# Revit family: 1030072(n0300)
name_source: partatom
category: Security Devices
units: mm (PartAtom-declared; Revit-internal decimal feet)

## family parameters
Always vertical = No
Cut with Voids When Loaded = No
Host = Ceiling
OmniClass Number = 23.85.30.14
OmniClass Title = Presence Detection/Registration
Room Calculation Point = No
Shared = Yes

## types (2) — shared parameters
zero-valued in all types: A

## per-type parameters (varying)
- Type 1: CTN=0; EF000008=0 mm  [stored 0 ft]; EF000040=0 mm  [stored 0 ft]; EF000049=0 mm  [stored 0 ft]; EF000194=0; EF000218=0 mm  [stored 0 ft]; EF000551=0 mm  [stored 0 ft]; EF000846=0 mm  [stored 0 ft]; EF001322=0 mm  [stored 0 ft]; EF001323=0 mm  [stored 0 ft]; EF003843=0 mm  [stored 0 ft]; EF003882=0; EF004101=0.00°; EF004265=0 mm  [stored 0 ft]; EF006589=0; EF006590=0; EF008011=0 mm  [stored 0 ft]; EF010886=0 mm  [stored 0 ft]; EF010945=0 mm  [stored 0 ft]; EF010946=0 mm  [stored 0 ft]; EF012278=0 mm  [stored 0 ft]; LOG=0; NOCUPEROU=0; PRICEQUANTITY=0; QUANTITYINT=0; QUANTITYMIN=0
- 1030072: ARTICLENO=NB; BOMINFO=LINA; CATALOG=Theben; COO=CN; CTN=85365080; DEEPLINK_PRODUKTSEITE=http://www.theben.de; DESCLONG=Passive infrared presence detector for flush or surface ceiling mounting, Rectangular detection area 360° for corridors, 28x5 m, (140 square meters) at 3 m mounting height (transverse walking), 14x5 m, (70 square meters) at 3 m mounting height (frontal walking), 1 channel light (relay 230 V), Can also be used in damp rooms and outdoors due to protection class IP 54, Remote controllable, Parallel connection with other LUXA 103 or theMura Slave possible, Switching capacity optimized for LED up to 400 W, Semi- or fully automatic operation, Integrated push button input, With pulse function, teach-in function, test function and staircase lighting function, Area restriction possible with cover clips, Housing color white; DESCSHORT=Corridor presence detector ceiling mounting flush-mounted/DE, detection area 28x5 m, 1 x light; EF000003=EV000383; EF000007=White; EF000008=80 mm  [stored 0.262467 ft]; EF000010=Presence detector; EF000025=true; EF000040=80 mm  [stored 0.262467 ft]; EF000049=80 mm  [stored 0.262467 ft]; EF000124=Plug-in clamp; EF000139=Untreated; EF000147=false; EF000187=AC; EF000194=15; EF000218=49 mm  [stored 0.160761 ft]; EF000416=50, 50 Hz; EF000483=false; EF000551=80 mm  [stored 0.262467 ft]; EF000846=40 mm  [stored 0.131234 ft]; EF001098=true; EF001099=true; EF001198=false; EF001257=Thermoplast; EF001322=14000 mm; EF001323=14000 mm; EF001731=-25, 55 °C; EF002169=Plastic; EF003429=true; EF003808=false; EF003814=5, 1000 lx; EF003832=false; EF003843=140000 mm; EF003848=true; EF003858=false; EF003863=false; EF003876=true; EF003882=9010; EF003890=true; EF003898=true; EF003904=true; EF003920=false; EF004101=360.00°; EF004265=40 mm  [stored 0.131234 ft]; EF004293=IK04; EF005474=IP54; EF005624=false; EF006243=false; EF006311=false; EF006569=matt; EF006582=0, 360 °; EF006589=15; EF006590=30; EF006644=false; EF007575=true; EF008011=3000 mm; EF009569=false; EF010886=31 mm  [stored 0.101706 ft]; EF010945=80 mm  [stored 0.262467 ft]; EF010946=60 mm  [stored 0.19685 ft]; EF011072=false; EF011991=false; EF012278=61 mm  [stored 0.200131 ft]; EF014925=false; EF014926=false; EF014927=false; EF020270=Passive infrared; EF021180=true; EF023790=false; GEBRAUCHSANLEITUNG=http://www.theben.de; INTNO=4003468101773; LINA=1030072; LOG=300; MANUID=1030072; MANUNAME=Theben AG; MANUTYPEDESC=LUXA 103 S360-100-28 DE-UP WH; Manufacturer=Theben; Model=1030072; NB=1030072(N0300); NBSYN=$MANUID.($SA.$A.$LOG.); NN=LUXA 103; NOCUPEROU=1; PRICEQUANTITY=1; PRODUKTDATENBLATT=http://www.theben.de; QUANTITYINT=1; QUANTITYMIN=1; REACH_ERKLAERUNG=http://www.theben.de; REMARKS=ERP-GROUP 450; SA=None; SUPPLIER=THEBEN; SUPPLIERALTNO=1030072

note: [stored X ft] marks values corroborated as IEEE doubles in the binary element streams (Revit-internal decimal feet)

## geometry (parser evidence)
native form markers: Sweep x12
no freeform markers — native parametric forms only
